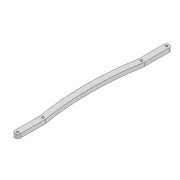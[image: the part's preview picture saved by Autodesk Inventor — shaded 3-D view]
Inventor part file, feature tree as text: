
AUTODESK INVENTOR PART (.ipt)
format: ipt  version: 2022 (Build 260153000, 153)  size: 104,960 bytes
history: native  units: mm
features: extrude x1, sketch x1
ambient origin geometry x8: Origin, YZ Plane, XZ Plane, XY Plane, X Axis, Y Axis, Z Axis, Center Point
bodies: Solid1 (feature_tree)
feature tree (2):
  extrude  "Extrusion1"  Depth=300.0mm
  sketch  "Sketch1"  dims[d0=2.2mm d1=2.2mm d2=6.0mm d3=153.89mm d6=4.0mm d7=0.0mm d10=2.2mm d11=25.907mm d12=2.2mm d13=127.773mm d16=300.0mm d17=300.0mm]
